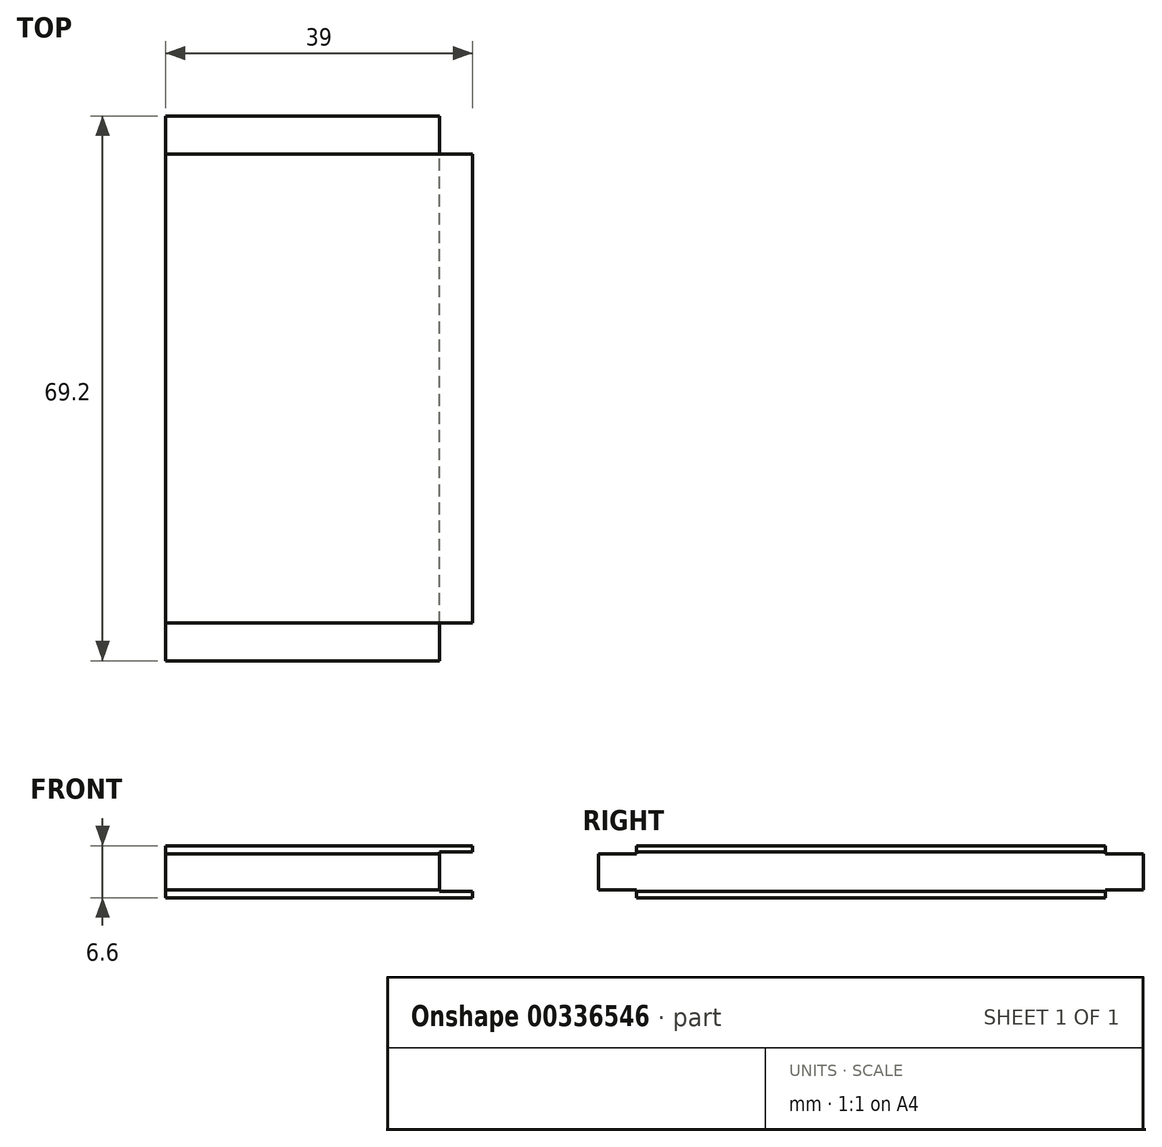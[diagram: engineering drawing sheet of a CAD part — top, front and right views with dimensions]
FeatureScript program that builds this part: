
annotation { "Feature Type Name" : "Feature", "Feature Type Description" : "" }
export const myFeature = defineFeature(function(context is Context, id is Id, definition is map)
    precondition{}
    {
        {
            var Q0;
            Q0=qCreatedBy(makeId("Front.planeOp"),FACE);
            var sketch = newSketch(context, id + "F0", { "sketchPlane" : qUnion([Q0])});
            skLineSegment(sketch, "E0.bottom", {"start": v(-21.16, 3.68) * mm, "end": v(17.84, 3.68) * mm});
            skLineSegment(sketch, "E0.top", {"start": v(-21.16, -2.92) * mm, "end": v(17.84, -2.92) * mm});
            skLineSegment(sketch, "E0.left", {"start": v(-21.16, 3.68) * mm, "end": v(-21.16, -2.92) * mm});
            skLineSegment(sketch, "E0.right", {"start": v(17.84, 3.68) * mm, "end": v(17.84, 2.88) * mm});
            skLineSegment(sketch, "E1.0", {"start": v(-21.16, 2.68) * mm, "end": v(13.64, 2.68) * mm});
            skLineSegment(sketch, "E2.0", {"start": v(-21.16, -1.92) * mm, "end": v(13.64, -1.92) * mm});
            skLineSegment(sketch, "E3.0", {"start": v(13.64, 3.68) * mm, "end": v(13.64, -2.92) * mm});
            skLineSegment(sketch, "E4.0", {"start": v(13.64, 2.88) * mm, "end": v(17.84, 2.88) * mm});
            skLineSegment(sketch, "E5.0", {"start": v(13.64, -2.12) * mm, "end": v(17.84, -2.12) * mm});
            skLineSegment(sketch, "E6.trimOffspring", {"start": v(17.84, -2.12) * mm, "end": v(17.84, -2.92) * mm});
            skSolve(sketch);
        }
        {
            var Q0;
            {var subQ0=sQuery(id+"F0.wireOp",EDGE,"E1.0");Q0=makeQuery(id+"F0.imprint","IMPRINT",FACE,{"disambiguationData":[TD([[makeQuery(id+"F0.imprint","IMPRINT",EDGE,{"derivedFrom":subQ0}),-1.0]])]});}
            extrude(context, id + "F1", {"entities" : qUnion([Q0]), "endBound" : BoundingType.SYMMETRIC, "depth" : 69.2 * mm});
        }
        {
            var Q0;
            {var subQ0=sQuery(id+"F0.wireOp",EDGE,"E1.0");Q0=makeQuery(id+"F0.imprint","IMPRINT",FACE,{"disambiguationData":[TD([[makeQuery(id+"F0.imprint","IMPRINT",EDGE,{"derivedFrom":subQ0}),1.0]])]});}
            var Q1;
            {var subQ1=sQuery(id+"F0.wireOp",EDGE,"E2.0");Q1=makeQuery(id+"F0.imprint","IMPRINT",FACE,{"disambiguationData":[TD([[makeQuery(id+"F0.imprint","IMPRINT",EDGE,{"derivedFrom":subQ1}),-1.0]])]});}
            var Q2;
            {var subQ4=sQuery(id+"F0.wireOp",EDGE,"E5.0");Q2=makeQuery(id+"F0.imprint","IMPRINT",FACE,{"disambiguationData":[TD([[makeQuery(id+"F0.imprint","IMPRINT",EDGE,{"derivedFrom":subQ4}),-1.0]])]});}
            var Q3;
            {var subQ0=sQuery(id+"F0.wireOp",EDGE,"E0.right");Q3=makeQuery(id+"F0.imprint","IMPRINT",FACE,{"disambiguationData":[TD([[makeQuery(id+"F0.imprint","IMPRINT",EDGE,{"derivedFrom":subQ0}),-1.0]])]});}
            extrude(context, id + "F2", {"entities" : qUnion([Q0, Q1, Q2, Q3]), "operationType" : NewBodyOperationType.ADD, "endBound" : BoundingType.SYMMETRIC, "depth" : 59.6 * mm});
        }
    });
